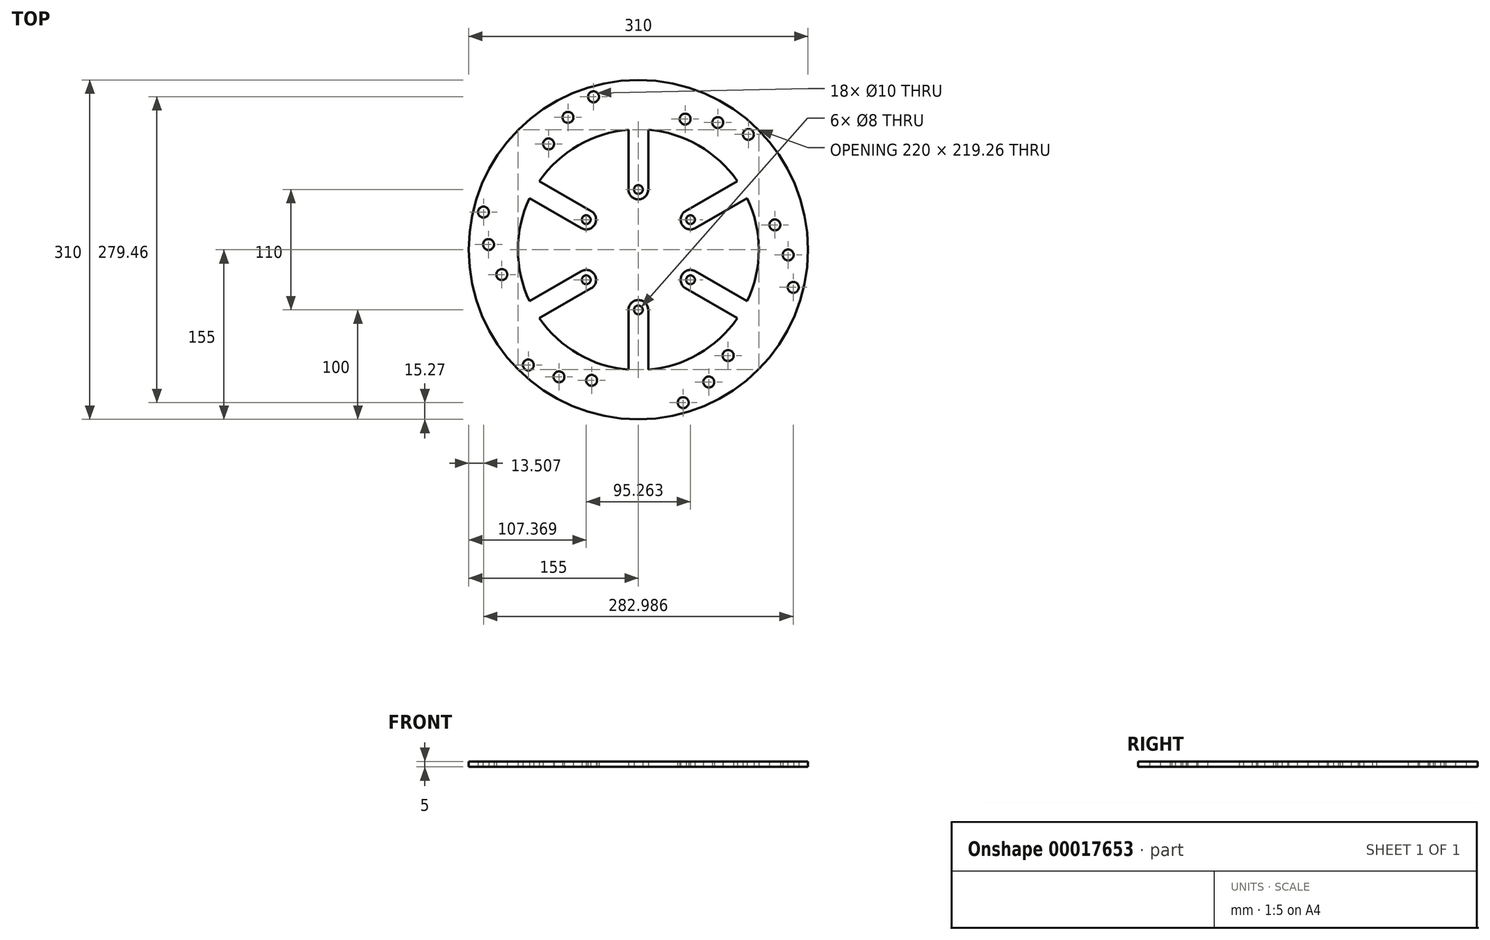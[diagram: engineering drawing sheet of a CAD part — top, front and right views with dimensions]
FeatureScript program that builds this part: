
annotation { "Feature Type Name" : "Feature", "Feature Type Description" : "" }
export const myFeature = defineFeature(function(context is Context, id is Id, definition is map)
    precondition{}
    {
        {
            var Q0;
            Q0=qCreatedBy(makeId("Top.planeOp"),FACE);
            var sketch = newSketch(context, id + "F0", { "sketchPlane" : qUnion([Q0])});
            skCircle(sketch, "E0", {"center": v(0, 0) * mm, "radius": 155 * mm});
            skCircle(sketch, "E1", {"center": v(0, 55) * mm, "radius": 4 * mm});
            skCircle(sketch, "E2", {"center": v(0, 55) * mm, "radius": 9 * mm});
            skCircle(sketch, "E3", {"center": v(0, 0) * mm, "radius": 46 * mm});
            skCircle(sketch, "E4", {"center": v(0, 0) * mm, "radius": 110 * mm});
            skLineSegment(sketch, "E5", {"start": v(0, 0) * mm, "end": v(-134.23, 77.5) * mm});
            skLineSegment(sketch, "E6", {"start": v(0, 0) * mm, "end": v(0, 155) * mm});
            skPoint(sketch, "E7.visualSharp", {"position": v(0, 110) * mm});
            skLineSegment(sketch, "E8", {"start": v(-9, 55) * mm, "end": v(-9, 109.63) * mm});
            skLineSegment(sketch, "E9", {"start": v(9, 55) * mm, "end": v(9, 109.63) * mm});
            skArc(sketch, "E10", {"start": v(0, 155) * mm, "mid": v(-64.32, 120.9) * mm, "end": v(-95.26, 55) * mm});
            skCircle(sketch, "E11", {"center": v(-64.32, 120.9) * mm, "radius": 5 * mm});
            skCircle(sketch, "E12", {"center": v(-40.97, 139.73) * mm, "radius": 5 * mm});
            skCircle(sketch, "E13", {"center": v(-82, 96.66) * mm, "radius": 5 * mm});
            skArc(sketch, "E14.1.0", {"start": v(-134.23, 77.5) * mm, "mid": v(-136.85, 4.75) * mm, "end": v(-95.26, -55) * mm});
            skCircle(sketch, "E14.1.1", {"center": v(-141.5, 34.39) * mm, "radius": 5 * mm});
            skCircle(sketch, "E14.1.2", {"center": v(-136.85, 4.75) * mm, "radius": 5 * mm});
            skCircle(sketch, "E14.1.3", {"center": v(-124.7, -22.68) * mm, "radius": 5 * mm});
            skLineSegment(sketch, "E14.1.4", {"start": v(-52.13, 19.7) * mm, "end": v(-99.44, 47.02) * mm});
            skLineSegment(sketch, "E14.1.5", {"start": v(-43.13, 35.3) * mm, "end": v(-90.44, 62.6) * mm});
            skCircle(sketch, "E14.1.6", {"center": v(-47.63, 27.5) * mm, "radius": 9 * mm});
            skCircle(sketch, "E14.1.7", {"center": v(-47.63, 27.5) * mm, "radius": 4 * mm});
            skArc(sketch, "E14.2.0", {"start": v(-134.23, -77.5) * mm, "mid": v(-72.54, -116.15) * mm, "end": v(0, -110) * mm});
            skCircle(sketch, "E14.2.1", {"center": v(-100.53, -105.34) * mm, "radius": 5 * mm});
            skCircle(sketch, "E14.2.2", {"center": v(-72.54, -116.15) * mm, "radius": 5 * mm});
            skCircle(sketch, "E14.2.3", {"center": v(-42.7, -119.34) * mm, "radius": 5 * mm});
            skLineSegment(sketch, "E14.2.4", {"start": v(-43.13, -35.3) * mm, "end": v(-90.44, -62.6) * mm});
            skLineSegment(sketch, "E14.2.5", {"start": v(-52.13, -19.7) * mm, "end": v(-99.44, -47.02) * mm});
            skCircle(sketch, "E14.2.6", {"center": v(-47.63, -27.5) * mm, "radius": 9 * mm});
            skCircle(sketch, "E14.2.7", {"center": v(-47.63, -27.5) * mm, "radius": 4 * mm});
            skArc(sketch, "E14.3.0", {"start": v(0, -155) * mm, "mid": v(64.32, -120.9) * mm, "end": v(95.26, -55) * mm});
            skCircle(sketch, "E14.3.1", {"center": v(40.97, -139.73) * mm, "radius": 5 * mm});
            skCircle(sketch, "E14.3.2", {"center": v(64.32, -120.9) * mm, "radius": 5 * mm});
            skCircle(sketch, "E14.3.3", {"center": v(82, -96.66) * mm, "radius": 5 * mm});
            skLineSegment(sketch, "E14.3.4", {"start": v(9, -55) * mm, "end": v(9, -109.63) * mm});
            skLineSegment(sketch, "E14.3.5", {"start": v(-9, -55) * mm, "end": v(-9, -109.63) * mm});
            skCircle(sketch, "E14.3.6", {"center": v(0, -55) * mm, "radius": 9 * mm});
            skCircle(sketch, "E14.3.7", {"center": v(0, -55) * mm, "radius": 4 * mm});
            skArc(sketch, "E14.4.0", {"start": v(134.23, -77.5) * mm, "mid": v(136.85, -4.75) * mm, "end": v(95.26, 55) * mm});
            skCircle(sketch, "E14.4.1", {"center": v(141.5, -34.39) * mm, "radius": 5 * mm});
            skCircle(sketch, "E14.4.2", {"center": v(136.85, -4.75) * mm, "radius": 5 * mm});
            skCircle(sketch, "E14.4.3", {"center": v(124.7, 22.68) * mm, "radius": 5 * mm});
            skLineSegment(sketch, "E14.4.4", {"start": v(52.13, -19.7) * mm, "end": v(99.44, -47.02) * mm});
            skLineSegment(sketch, "E14.4.5", {"start": v(43.13, -35.3) * mm, "end": v(90.44, -62.6) * mm});
            skCircle(sketch, "E14.4.6", {"center": v(47.63, -27.5) * mm, "radius": 9 * mm});
            skCircle(sketch, "E14.4.7", {"center": v(47.63, -27.5) * mm, "radius": 4 * mm});
            skArc(sketch, "E14.5.0", {"start": v(134.23, 77.5) * mm, "mid": v(72.54, 116.15) * mm, "end": v(0, 110) * mm});
            skCircle(sketch, "E14.5.1", {"center": v(100.53, 105.34) * mm, "radius": 5 * mm});
            skCircle(sketch, "E14.5.2", {"center": v(72.54, 116.15) * mm, "radius": 5 * mm});
            skCircle(sketch, "E14.5.3", {"center": v(42.7, 119.34) * mm, "radius": 5 * mm});
            skLineSegment(sketch, "E14.5.4", {"start": v(43.13, 35.3) * mm, "end": v(90.44, 62.6) * mm});
            skLineSegment(sketch, "E14.5.5", {"start": v(52.13, 19.7) * mm, "end": v(99.44, 47.02) * mm});
            skCircle(sketch, "E14.5.6", {"center": v(47.63, 27.5) * mm, "radius": 9 * mm});
            skCircle(sketch, "E14.5.7", {"center": v(47.63, 27.5) * mm, "radius": 4 * mm});
            skLineSegment(sketch, "E15", {"start": v(0, 0) * mm, "end": v(-134.23, -77.5) * mm});
            skSolve(sketch);
        }
        {
            var Q0;
            {var subQ7=sQuery(id+"F0.wireOp",EDGE,"E4");var subQ16=makeQuery(id+"F0.imprint","INTERSECT",VERTEX,{"derivedFrom":[subQ7,sQuery(id+"F0.wireOp",EDGE,"E8")]});Q0=makeQuery(id+"F0.imprint","IMPRINT",FACE,{"disambiguationData":[TD([[makeQuery(id+"F0.imprint","IMPRINT",EDGE,{"disambiguationData":[TD([[subQ16,-1.0]])],"derivedFrom":subQ7}),-1.0]])]});}
            var Q1;
            {var subQ0=sQuery(id+"F0.wireOp",EDGE,"E12");var subQ1=sQuery(id+"F0.wireOp",EDGE,"E10");var subQ2=makeQuery(id+"F0.imprint","INTERSECT",VERTEX,{"disambiguationData":[OD(1.0)],"derivedFrom":[subQ1,subQ0]});Q1=makeQuery(id+"F0.imprint","IMPRINT",FACE,{"disambiguationData":[TD([[makeQuery(id+"F0.imprint","IMPRINT",EDGE,{"disambiguationData":[TD([[subQ2,-1.0]])],"derivedFrom":subQ1}),-1.0]])]});}
            var Q2;
            {var subQ1=sQuery(id+"F0.wireOp",EDGE,"E14.5.0");var subQ12=sQuery(id+"F0.wireOp",EDGE,"E0");var subQ13=makeQuery(id+"F0.imprint","INTERSECT",VERTEX,{"derivedFrom":[subQ12,subQ1]});Q2=makeQuery(id+"F0.imprint","IMPRINT",FACE,{"disambiguationData":[TD([[makeQuery(id+"F0.imprint","IMPRINT",EDGE,{"disambiguationData":[TD([[subQ13,-1.0]])],"derivedFrom":subQ1}),-1.0]])]});}
            var Q3;
            {var subQ12=sQuery(id+"F0.wireOp",EDGE,"E0");var subQ15=sQuery(id+"F0.wireOp",EDGE,"E14.4.0");var subQ25=makeQuery(id+"F0.imprint","INTERSECT",VERTEX,{"derivedFrom":[subQ12,subQ15]});Q3=makeQuery(id+"F0.imprint","IMPRINT",FACE,{"disambiguationData":[TD([[makeQuery(id+"F0.imprint","IMPRINT",EDGE,{"disambiguationData":[TD([[subQ25,-1.0]])],"derivedFrom":subQ12}),1.0]])]});}
            var Q4;
            {var subQ11=sQuery(id+"F0.wireOp",EDGE,"E0");var subQ14=sQuery(id+"F0.wireOp",EDGE,"E14.3.0");var subQ23=makeQuery(id+"F0.imprint","INTERSECT",VERTEX,{"derivedFrom":[subQ11,subQ14]});Q4=makeQuery(id+"F0.imprint","IMPRINT",FACE,{"disambiguationData":[TD([[makeQuery(id+"F0.imprint","IMPRINT",EDGE,{"disambiguationData":[TD([[subQ23,-1.0]])],"derivedFrom":subQ11}),1.0]])]});}
            var Q5;
            {var subQ10=sQuery(id+"F0.wireOp",EDGE,"E4");var subQ15=sQuery(id+"F0.wireOp",EDGE,"E14.2.0");var subQ18=makeQuery(id+"F0.imprint","INTERSECT",VERTEX,{"derivedFrom":[subQ10,subQ15]});Q5=makeQuery(id+"F0.imprint","IMPRINT",FACE,{"disambiguationData":[TD([[makeQuery(id+"F0.imprint","IMPRINT",EDGE,{"disambiguationData":[TD([[subQ18,-1.0]])],"derivedFrom":subQ10}),-1.0]])]});}
            var Q6;
            {var subQ3=sQuery(id+"F0.wireOp",EDGE,"E4");var subQ16=makeQuery(id+"F0.imprint","INTERSECT",VERTEX,{"derivedFrom":[subQ3,sQuery(id+"F0.wireOp",EDGE,"E14.2.4")]});Q6=makeQuery(id+"F0.imprint","IMPRINT",FACE,{"disambiguationData":[TD([[makeQuery(id+"F0.imprint","IMPRINT",EDGE,{"disambiguationData":[TD([[subQ16,-1.0]])],"derivedFrom":subQ3}),-1.0]])]});}
            var Q7;
            {var subQ3=sQuery(id+"F0.wireOp",EDGE,"E14.1.0");var subQ8=sQuery(id+"F0.wireOp",EDGE,"E14.1.1");var subQ9=makeQuery(id+"F0.imprint","INTERSECT",VERTEX,{"disambiguationData":[OD(1.0)],"derivedFrom":[subQ3,subQ8]});Q7=makeQuery(id+"F0.imprint","IMPRINT",FACE,{"disambiguationData":[TD([[makeQuery(id+"F0.imprint","IMPRINT",EDGE,{"disambiguationData":[TD([[subQ9,-1.0]])],"derivedFrom":subQ3}),-1.0]])]});}
            var Q8;
            {var subQ10=sQuery(id+"F0.wireOp",EDGE,"E4");var subQ16=makeQuery(id+"F0.imprint","INTERSECT",VERTEX,{"derivedFrom":[subQ10,sQuery(id+"F0.wireOp",EDGE,"E14.1.4")]});Q8=makeQuery(id+"F0.imprint","IMPRINT",FACE,{"disambiguationData":[TD([[makeQuery(id+"F0.imprint","IMPRINT",EDGE,{"disambiguationData":[TD([[subQ16,-1.0]])],"derivedFrom":subQ10}),-1.0]])]});}
            extrude(context, id + "F1", {"entities" : qUnion([Q0, Q1, Q2, Q3, Q4, Q5, Q6, Q7, Q8]), "depth" : 5 * mm});
        }
        {
            var Q0;
            {var subQ3=sQuery(id+"F0.wireOp",EDGE,"E14.1.5");Q0=makeQuery(id+"F0.imprint","IMPRINT",FACE,{"disambiguationData":[TD([[makeQuery(id+"F0.imprint","IMPRINT",EDGE,{"derivedFrom":subQ3}),1.0]])]});}
            var Q1;
            {var subQ3=sQuery(id+"F0.wireOp",EDGE,"E14.1.4");Q1=makeQuery(id+"F0.imprint","IMPRINT",FACE,{"disambiguationData":[TD([[makeQuery(id+"F0.imprint","IMPRINT",EDGE,{"derivedFrom":subQ3}),-1.0]])]});}
            var Q2;
            {var subQ0=sQuery(id+"F0.wireOp",EDGE,"E14.1.7");var subQ1=sQuery(id+"F0.wireOp",EDGE,"E5");var subQ2=makeQuery(id+"F0.imprint","INTERSECT",VERTEX,{"disambiguationData":[OD(1.0)],"derivedFrom":[subQ1,subQ0]});Q2=makeQuery(id+"F0.imprint","IMPRINT",FACE,{"disambiguationData":[TD([[makeQuery(id+"F0.imprint","IMPRINT",EDGE,{"disambiguationData":[TD([[subQ2,-1.0]])],"derivedFrom":subQ1}),1.0]])]});}
            var Q3;
            {var subQ0=sQuery(id+"F0.wireOp",EDGE,"E14.1.7");var subQ1=sQuery(id+"F0.wireOp",EDGE,"E5");var subQ2=makeQuery(id+"F0.imprint","INTERSECT",VERTEX,{"disambiguationData":[OD(1.0)],"derivedFrom":[subQ1,subQ0]});Q3=makeQuery(id+"F0.imprint","IMPRINT",FACE,{"disambiguationData":[TD([[makeQuery(id+"F0.imprint","IMPRINT",EDGE,{"disambiguationData":[TD([[subQ2,-1.0]])],"derivedFrom":subQ1}),-1.0]])]});}
            var Q4;
            {var subQ1=sQuery(id+"F0.wireOp",EDGE,"E14.2.6");var subQ6=makeQuery(id+"F0.imprint","INTERSECT",VERTEX,{"derivedFrom":[sQuery(id+"F0.wireOp",EDGE,"E14.2.5"),subQ1]});Q4=makeQuery(id+"F0.imprint","IMPRINT",FACE,{"disambiguationData":[TD([[makeQuery(id+"F0.imprint","IMPRINT",EDGE,{"disambiguationData":[TD([[subQ6,-1.0]])],"derivedFrom":subQ1}),1.0]])]});}
            var Q5;
            {var subQ5=sQuery(id+"F0.wireOp",EDGE,"E14.2.5");Q5=makeQuery(id+"F0.imprint","IMPRINT",FACE,{"disambiguationData":[TD([[makeQuery(id+"F0.imprint","IMPRINT",EDGE,{"derivedFrom":subQ5}),1.0]])]});}
            var Q6;
            {var subQ5=sQuery(id+"F0.wireOp",EDGE,"E14.2.4");Q6=makeQuery(id+"F0.imprint","IMPRINT",FACE,{"disambiguationData":[TD([[makeQuery(id+"F0.imprint","IMPRINT",EDGE,{"derivedFrom":subQ5}),-1.0]])]});}
            var Q7;
            {var subQ0=sQuery(id+"F0.wireOp",EDGE,"E6");var subQ3=sQuery(id+"F0.wireOp",EDGE,"E1");var subQ6=makeQuery(id+"F0.imprint","INTERSECT",VERTEX,{"disambiguationData":[OD(0.0)],"derivedFrom":[subQ3,subQ0]});Q7=makeQuery(id+"F0.imprint","IMPRINT",FACE,{"disambiguationData":[TD([[makeQuery(id+"F0.imprint","IMPRINT",EDGE,{"disambiguationData":[TD([[subQ6,1.0]])],"derivedFrom":subQ3}),-1.0]])]});}
            var Q8;
            {var subQ0=sQuery(id+"F0.wireOp",EDGE,"E8");Q8=makeQuery(id+"F0.imprint","IMPRINT",FACE,{"disambiguationData":[TD([[makeQuery(id+"F0.imprint","IMPRINT",EDGE,{"derivedFrom":subQ0}),-1.0]])]});}
            var Q9;
            {var subQ0=sQuery(id+"F0.wireOp",EDGE,"E6");var subQ3=sQuery(id+"F0.wireOp",EDGE,"E1");var subQ6=makeQuery(id+"F0.imprint","INTERSECT",VERTEX,{"disambiguationData":[OD(0.0)],"derivedFrom":[subQ3,subQ0]});Q9=makeQuery(id+"F0.imprint","IMPRINT",FACE,{"disambiguationData":[TD([[makeQuery(id+"F0.imprint","IMPRINT",EDGE,{"disambiguationData":[TD([[subQ6,-1.0]])],"derivedFrom":subQ3}),-1.0]])]});}
            var Q10;
            {var subQ0=sQuery(id+"F0.wireOp",EDGE,"E9");Q10=makeQuery(id+"F0.imprint","IMPRINT",FACE,{"disambiguationData":[TD([[makeQuery(id+"F0.imprint","IMPRINT",EDGE,{"derivedFrom":subQ0}),1.0]])]});}
            var Q11;
            {var subQ2=sQuery(id+"F0.wireOp",EDGE,"E14.5.4");Q11=makeQuery(id+"F0.imprint","IMPRINT",FACE,{"disambiguationData":[TD([[makeQuery(id+"F0.imprint","IMPRINT",EDGE,{"derivedFrom":subQ2}),-1.0]])]});}
            var Q12;
            Q12=makeQuery(id+"F0.imprint","IMPRINT",FACE,{"disambiguationData":[TD([[makeQuery(id+"F0.imprint","IMPRINT",EDGE,{"derivedFrom":sQuery(id+"F0.wireOp",EDGE,"E14.5.7")}),-1.0]])]});
            var Q13;
            Q13=makeQuery(id+"F0.imprint","IMPRINT",FACE,{"disambiguationData":[TD([[makeQuery(id+"F0.imprint","IMPRINT",EDGE,{"derivedFrom":sQuery(id+"F0.wireOp",EDGE,"E14.4.7")}),-1.0]])]});
            var Q14;
            {var subQ2=sQuery(id+"F0.wireOp",EDGE,"E14.4.4");Q14=makeQuery(id+"F0.imprint","IMPRINT",FACE,{"disambiguationData":[TD([[makeQuery(id+"F0.imprint","IMPRINT",EDGE,{"derivedFrom":subQ2}),-1.0]])]});}
            var Q15;
            {var subQ3=sQuery(id+"F0.wireOp",EDGE,"E14.2.6");var subQ7=makeQuery(id+"F0.imprint","INTERSECT",VERTEX,{"derivedFrom":[sQuery(id+"F0.wireOp",EDGE,"E14.2.4"),subQ3]});Q15=makeQuery(id+"F0.imprint","IMPRINT",FACE,{"disambiguationData":[TD([[makeQuery(id+"F0.imprint","IMPRINT",EDGE,{"disambiguationData":[TD([[subQ7,1.0]])],"derivedFrom":subQ3}),1.0]])]});}
            var Q16;
            Q16=makeQuery(id+"F0.imprint","IMPRINT",FACE,{"disambiguationData":[TD([[makeQuery(id+"F0.imprint","IMPRINT",EDGE,{"derivedFrom":sQuery(id+"F0.wireOp",EDGE,"E14.3.7")}),-1.0]])]});
            var Q17;
            {var subQ2=sQuery(id+"F0.wireOp",EDGE,"E14.3.4");Q17=makeQuery(id+"F0.imprint","IMPRINT",FACE,{"disambiguationData":[TD([[makeQuery(id+"F0.imprint","IMPRINT",EDGE,{"derivedFrom":subQ2}),-1.0]])]});}
            extrude(context, id + "F2", {"entities" : qUnion([Q0, Q1, Q2, Q3, Q4, Q5, Q6, Q7, Q8, Q9, Q10, Q11, Q12, Q13, Q14, Q15, Q16, Q17]), "operationType" : NewBodyOperationType.ADD, "depth" : 5 * mm});
        }
    });
